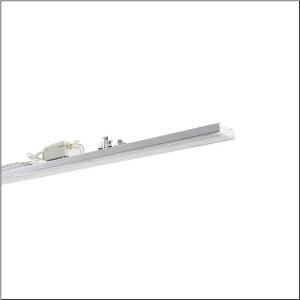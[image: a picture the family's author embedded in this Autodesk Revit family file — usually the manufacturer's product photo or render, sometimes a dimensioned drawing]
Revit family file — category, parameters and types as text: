
# Revit family: licross_r__21_recessed_mo_52tl19de445g_6927
name_source: partatom
category: Lighting Fixtures
units: mm (PartAtom-declared; Revit-internal decimal feet)

## family parameters
Cut with Voids When Loaded = No
Host = Face
Light Source = No
Part Type = Normal
Room Calculation Point = No
Round Connector Dimension = Use Diameter
Shared = No

## types (1)
- --- (1 x LED, 4930 lm, 29.9 W, 4000K)
    Apparent Load = 30 VA
    CIE Flux Codes = 55 90 98 100 100
    Color Rendering = 80
    Color Temperature = 4000K
    Default Elevation = 1800 mm
    Description = Licross® 21 Recessed MO, luminaire insert, of sheet steel, galvanised, coil coated, white, length: 750mm, width: 66mm, height: 67mm, LED rated luminous flux: 4.930lm, light colour: 840, control gear: DALI 2, with plug, 5-pole, with phase selection, mains connection: 220..240V, AC, 50/60Hz, rated input power: 30W, halogen-free wiring, primary light control with lens, of plastic, primary optical cover: cover, of PMMA, light emission: direct distribution, primary light characteristic: double asymmetric, protection rating (complete): IP40, insulation class (complete): insulation class I (protective earthing), certification: CE, ENEC, VDE, UKCA, protection symbol: D if used in an environment without relevant dust loads with corresponding accessories, impact resistance: IK06, permissible ambient temperature for indoor applications: -25..+35°C, corresponds to IFS (International Featured Standards) requirements for safety and quality in the food industry, reducing of maximum allowable ambient temperature of 5°C with ceiling mounting, LABS conformity tested according to VDMA 24364:2018-05, packaging unit: 1 piece
    Height = 58 mm
    Lamp = 1 x LED
    Lamp Light Flux = 4930 lm
    Lamp Power = 29.9 W
    Lamp count = 1
    Length = 750 mm
    Luminous efficacy = 165 lm/W
    Manufacturer = Siteco
    ModVariant = No
    Model = 52TL19DE445G
    Mounting Place = Ceiling
    Mounting Type = Pendant
    Number of Poles = 1
    OnlyDefault = Yes
    Power Factor = 1
    Product Name = Licross® 21 Recessed MO
    Product group = luminaire insert
    ProductGroupID = 901
    Protection Class = Protection class I
    Protection Degree = IP 40
    RLX_Detail_Level = 1
    RLX_Emergency_Light_Flux = 0 lm
    RLX_Emergency_Type = 0
    RLX_Emergency_Type_DB = No
    RlxData = <blob elided: 28605 chars, md5=0330c709>
    Socket = socket
    Standby Power = 0 W
    System Light Flux = 4930 lm
    System Power = 30 W
    Type Comments = factory setting: luminous flux: 100 % | dim-lin: 254 | 390 mA
    Type Image = l_1296930.jpg
    URL = http://relux.com
    VarID = @adj_059703
    Voltage = 0 V
    Weight = 0.00 kg
    Width = 66 mm

## geometry (parser evidence)
native form markers: Blend x4, Sweep x9
no freeform markers — native parametric forms only
